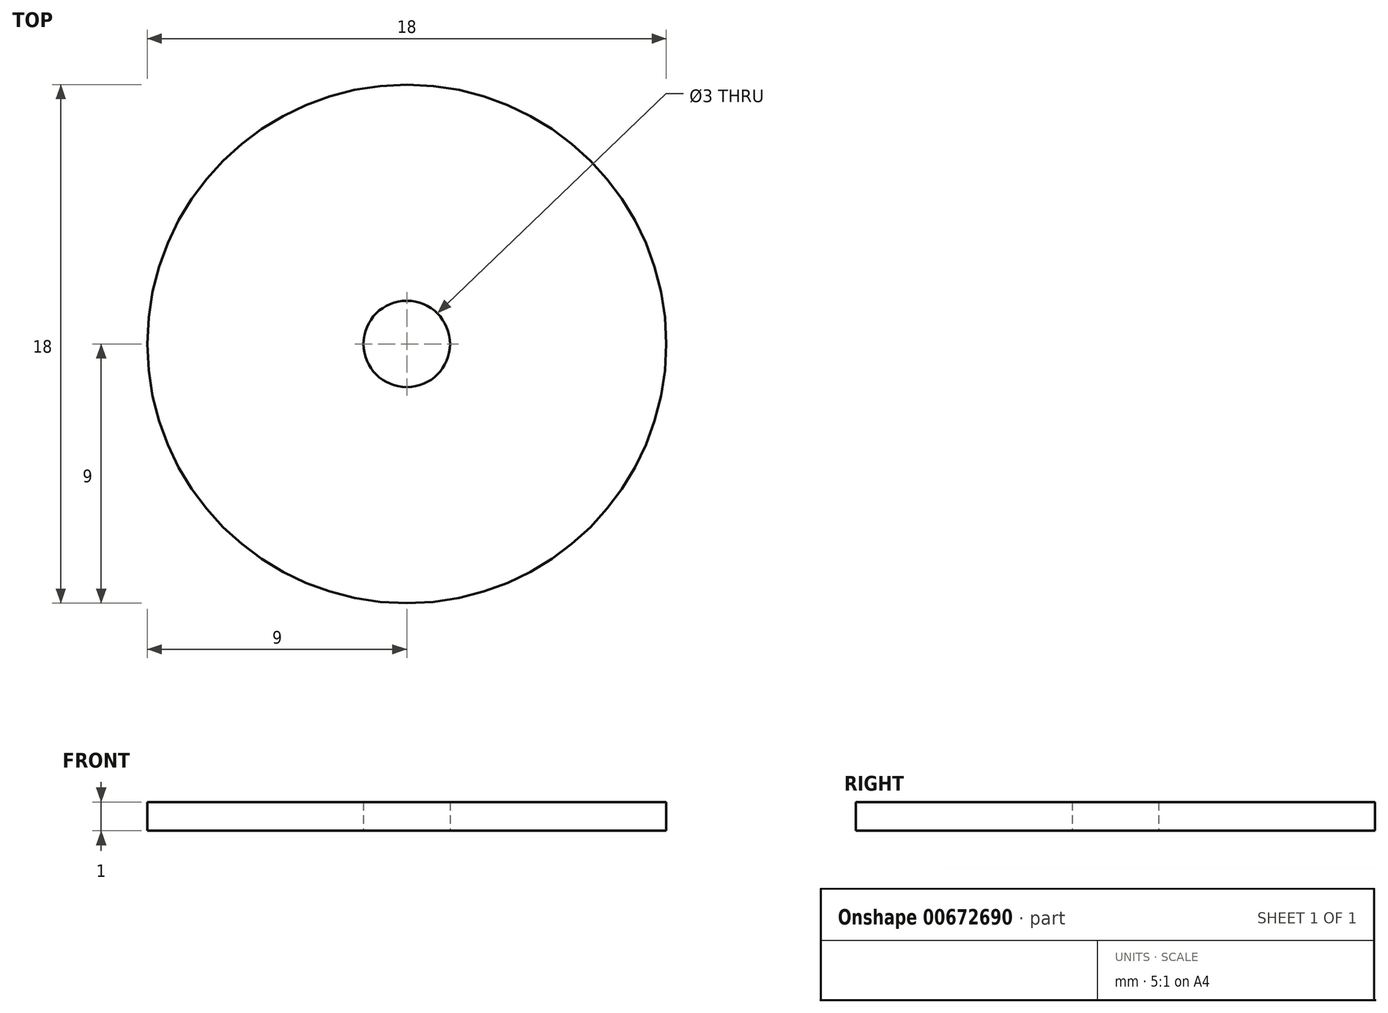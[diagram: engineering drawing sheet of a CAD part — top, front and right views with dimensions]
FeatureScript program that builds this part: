
annotation { "Feature Type Name" : "Feature", "Feature Type Description" : "" }
export const myFeature = defineFeature(function(context is Context, id is Id, definition is map)
    precondition{}
    {
        {
            var Q0;
            Q0=qCreatedBy(makeId("Top.planeOp"),FACE);
            var sketch = newSketch(context, id + "F0", { "sketchPlane" : qUnion([Q0])});
            skCircle(sketch, "E0", {"center": v(0, 0) * mm, "radius": 9 * mm});
            skCircle(sketch, "E1", {"center": v(0, 0) * mm, "radius": 1.5 * mm});
            skSolve(sketch);
        }
        {
            var Q0;
            Q0=makeQuery(id+"F0.imprint","IMPRINT",FACE,{"disambiguationData":[TD([[makeQuery(id+"F0.imprint","IMPRINT",EDGE,{"derivedFrom":sQuery(id+"F0.wireOp",EDGE,"E0")}),1.0]])]});
            extrude(context, id + "F1", {"entities" : qUnion([Q0]), "depth" : 1 * mm, "offsetDistance" : 25 * mm});
        }
    });
